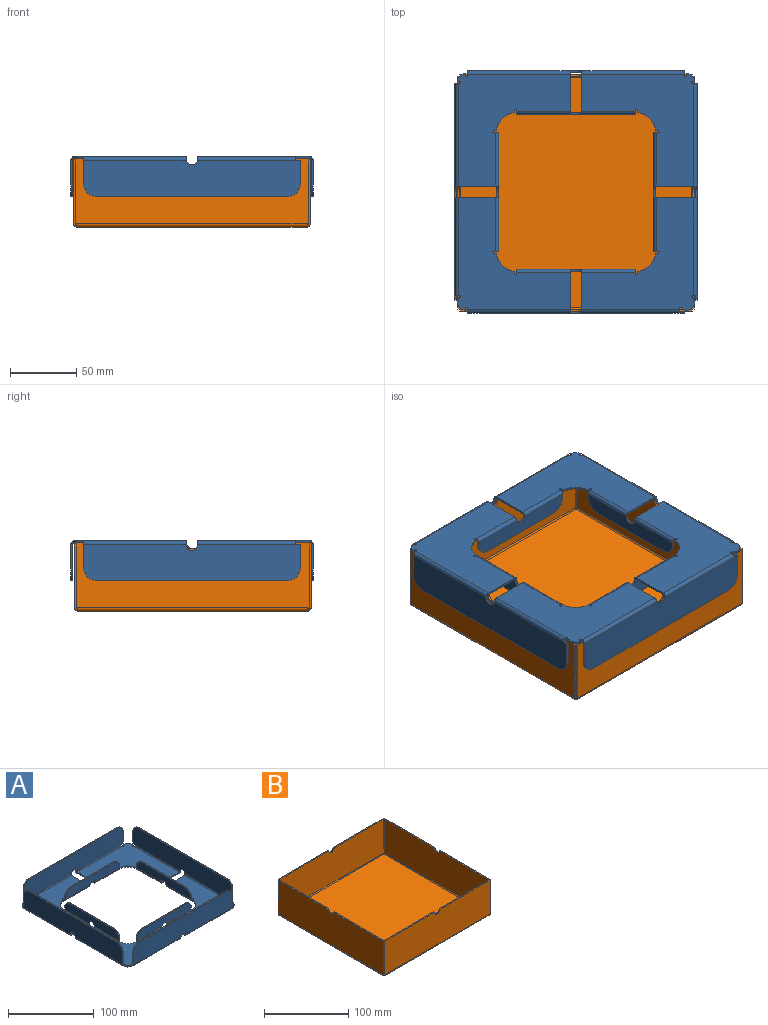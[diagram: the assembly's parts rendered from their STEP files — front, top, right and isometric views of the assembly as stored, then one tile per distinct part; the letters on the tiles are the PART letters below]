
ASSEMBLY  parts=2 mates=1
PART A: 225 faces, bbox 183x183x30 mm
  f0: plane 1.5x0.11mm, normal (-1,0,0), area 0.2mm2, adj f6,f7,f12,f105
  f1: plane 1.5x0.11mm, normal (-1,0,0), area 0.2mm2, adj f51,f52,f56,f96
  f2: cylinder r=15mm len=13.32mm, axis (0,0,-1), area 30.6mm2, adj f6,f7,f21,f24
  f3: plane 2.28x1.5mm, normal (0,1,0), area 3.4mm2, adj f6,f7,f9,f17
  f4: plane 1.5x0.11mm, normal (1,0,0), area 0.2mm2, adj f6,f7,f12,f83
  f5: plane 2.28x1.5mm, normal (1,0,0), area 3.4mm2, adj f6,f7,f8,f15
  f6: plane 85.61x85.5mm, normal (0,0,-1), area 4020mm2, adj f0,f2,f3,f4,f5,f8,f9,f10
  f7: plane 85.61x85.5mm, normal (0,0,1), area 4020mm2, adj f0,f2,f3,f4,f5,f8,f9,f10
  f8: plane 1.5x1mm, normal (0,-1,0), area 1.5mm2, adj f5,f6,f7,f11
  f9: plane 1.5x1mm, normal (-1,0,0), area 1.5mm2, adj f3,f6,f7,f11
  f10: plane 28x1.5mm, normal (-1,0,0), area 42mm2, adj f6,f7,f26,f44
  f11: cylinder r=8mm len=8mm, axis (0,0,-1), area 18.8mm2, adj f6,f7,f8,f9
  f12: plane 28x1.5mm, normal (0,-1,0), area 42mm2, adj f0,f4,f6,f7
  f13: cylinder r=0.8mm len=1.59mm, axis (0,0,1), area 3.8mm2, adj f6,f7,f14,f15
  f14: plane 1.5x0.7mm, normal (0,1,0), area 1.1mm2, adj f6,f7,f13,f84
  f15: plane 1.5x0.7mm, normal (0,-1,0), area 1.1mm2, adj f5,f6,f7,f13
  f16: cylinder r=0.8mm len=1.59mm, axis (0,0,1), area 3.8mm2, adj f6,f7,f17,f18
  f17: plane 1.5x0.7mm, normal (-1,0,0), area 1.1mm2, adj f3,f6,f7,f16
  f18: plane 1.5x0.7mm, normal (1,0,0), area 1.1mm2, adj f6,f7,f16,f25
  f19: plane 1.5x0.7mm, normal (1,0,0), area 1.1mm2, adj f6,f7,f20,f45
  f20: cylinder r=0.8mm len=1.59mm, axis (0,0,1), area 3.8mm2, adj f6,f7,f19,f21
  f21: plane 1.79x1.5mm, normal (-1,0,0), area 2.7mm2, adj f2,f6,f7,f20
  f22: cylinder r=0.8mm len=1.59mm, axis (0,0,1), area 3.8mm2, adj f6,f7,f23,f24
  f23: plane 1.5x0.7mm, normal (0,1,0), area 1.1mm2, adj f6,f7,f22,f104
  f24: plane 1.79x1.5mm, normal (0,-1,0), area 2.7mm2, adj f2,f6,f7,f22
  f25: plane 2.5x2.5mm, normal (1,0,0), area 4.1mm2, adj f18,f27,f28,f30
  f26: plane 2.5x2.5mm, normal (-1,0,0), area 4.1mm2, adj f10,f27,f28,f34
  f27: cylinder r=2.5mm len=73.63mm, axis (1,0,0), area 289.1mm2, adj f6,f25,f26,f36
  f28: cylinder r=1mm len=73.63mm, axis (1,0,0), area 115.7mm2, adj f7,f25,f26,f37
  f29: plane 1.5x0.11mm, normal (0,0,-1), area 0.2mm2, adj f35,f36,f37,f40
  f30: plane 3.87x1.5mm, normal (0,0,-1), area 5.8mm2, adj f25,f33,f36,f37
  f31: plane 17.5x1.5mm, normal (-1,0,0), area 26.2mm2, adj f36,f37,f39,f41
  f32: plane 144x1.5mm, normal (0,0,1), area 216mm2, adj f36,f37,f38,f39
  f33: plane 17.5x1.5mm, normal (1,0,0), area 26.2mm2, adj f30,f36,f37,f38
  f34: plane 1.5x0.11mm, normal (0,0,-1), area 0.2mm2, adj f26,f35,f36,f37
  f35: cylinder r=4.5mm len=8.78mm, axis (0,1,0), area 18.2mm2, adj f29,f34,f36,f37
  f36: plane 164x27.5mm, normal (0,1,0), area 4444.2mm2, adj f27,f29,f30,f31,f32,f33,f34,f35
  f37: plane 164x27.5mm, normal (0,-1,0), area 4444.2mm2, adj f28,f29,f30,f31,f32,f33,f34,f35
  f38: cylinder r=10mm len=10mm, axis (0,1,0), area 23.6mm2, adj f32,f33,f36,f37
  f39: cylinder r=10mm len=10mm, axis (0,1,0), area 23.6mm2, adj f31,f32,f36,f37
  f40: plane 2.5x2.5mm, normal (1,0,0), area 4.1mm2, adj f29,f42,f43,f54
  f41: plane 2.5x2.5mm, normal (-1,0,0), area 4.1mm2, adj f31,f42,f43,f63
  f42: cylinder r=2.5mm len=77.5mm, axis (1,0,0), area 304.3mm2, adj f36,f40,f41,f51
  f43: cylinder r=1mm len=77.5mm, axis (1,0,0), area 121.7mm2, adj f37,f40,f41,f52
  f44: plane 2.5x2.5mm, normal (-1,0,0), area 4.1mm2, adj f10,f46,f47,f73
  f45: plane 2.5x2.5mm, normal (1,0,0), area 4.1mm2, adj f19,f46,f47,f74
  f46: cylinder r=2.5mm len=40.5mm, axis (-1,0,0), area 159mm2, adj f6,f44,f45,f79
  f47: cylinder r=1mm len=40.5mm, axis (-1,0,0), area 63.6mm2, adj f7,f44,f45,f80
  f48: plane 2.28x1.5mm, normal (-1,0,0), area 3.4mm2, adj f51,f52,f53,f67
  f49: cylinder r=8mm len=7.84mm, axis (0,0,-1), area 16.4mm2, adj f51,f52,f53,f65
  f50: cylinder r=15mm len=13.32mm, axis (0,0,-1), area 30.6mm2, adj f51,f52,f59,f62
  f51: plane 85.5x85.45mm, normal (0,0,-1), area 4018.4mm2, adj f1,f42,f48,f49,f50,f53,f54,f55
  f52: plane 85.5x85.45mm, normal (0,0,1), area 4018.4mm2, adj f1,f43,f48,f49,f50,f53,f54,f55
  f53: plane 1.5x1mm, normal (0,-1,0), area 1.5mm2, adj f48,f49,f51,f52
  f54: plane 28x1.5mm, normal (1,0,0), area 42mm2, adj f40,f51,f52,f70
  f55: plane 1.5x0.11mm, normal (1,0,0), area 0.2mm2, adj f51,f52,f56,f100
  f56: plane 28x1.5mm, normal (0,-1,0), area 42mm2, adj f1,f51,f52,f55
  f57: plane 1.5x0.7mm, normal (0,1,0), area 1.1mm2, adj f51,f52,f58,f101
  f58: cylinder r=0.8mm len=1.59mm, axis (0,0,1), area 3.8mm2, adj f51,f52,f57,f59
  f59: plane 1.79x1.5mm, normal (0,-1,0), area 2.7mm2, adj f50,f51,f52,f58
  f60: cylinder r=0.8mm len=1.59mm, axis (0,0,1), area 3.8mm2, adj f51,f52,f61,f62
  f61: plane 1.5x0.7mm, normal (-1,0,0), area 1.1mm2, adj f51,f52,f60,f69
  f62: plane 1.79x1.5mm, normal (1,0,0), area 2.7mm2, adj f50,f51,f52,f60
  f63: plane 1.5x0.7mm, normal (-1,0,0), area 1.1mm2, adj f41,f51,f52,f64
  f64: cylinder r=0.8mm len=1.59mm, axis (0,0,1), area 3.8mm2, adj f51,f52,f63,f65
  f65: plane 1.54x1.5mm, normal (1,0,0), area 2.3mm2, adj f49,f51,f52,f64
  f66: cylinder r=0.8mm len=1.59mm, axis (0,0,1), area 3.8mm2, adj f51,f52,f67,f68
  f67: plane 1.5x0.7mm, normal (0,-1,0), area 1.1mm2, adj f48,f51,f52,f66
  f68: plane 1.5x0.7mm, normal (0,1,0), area 1.1mm2, adj f51,f52,f66,f97
  f69: plane 2.5x2.5mm, normal (-1,0,0), area 4.1mm2, adj f61,f71,f72,f76
  f70: plane 2.5x2.5mm, normal (1,0,0), area 4.1mm2, adj f54,f71,f72,f77
  f71: cylinder r=2.5mm len=40.5mm, axis (-1,0,0), area 159mm2, adj f51,f69,f70,f79
  f72: cylinder r=1mm len=40.5mm, axis (-1,0,0), area 63.6mm2, adj f52,f69,f70,f80
  f73: plane 1.5x0.11mm, normal (0,0,-1), area 0.2mm2, adj f44,f78,f79,f80
  f74: plane 2.5x1.5mm, normal (1,0,0), area 3.8mm2, adj f45,f79,f80,f81
  f75: plane 70x1.5mm, normal (0,0,1), area 105mm2, adj f79,f80,f81,f82
  f76: plane 2.5x1.5mm, normal (-1,0,0), area 3.8mm2, adj f69,f79,f80,f82
  f77: plane 1.5x0.11mm, normal (0,0,-1), area 0.2mm2, adj f70,f78,f79,f80
  f78: cylinder r=4.5mm len=8.78mm, axis (0,-1,0), area 18.2mm2, adj f73,f77,f79,f80
  f79: plane 90x12.5mm, normal (0,-1,0), area 1059.2mm2, adj f46,f71,f73,f74,f75,f76,f77,f78
  f80: plane 90x12.5mm, normal (0,1,0), area 1059.2mm2, adj f47,f72,f73,f74,f75,f76,f77,f78
  f81: cylinder r=10mm len=10mm, axis (0,-1,0), area 23.6mm2, adj f74,f75,f79,f80
  f82: cylinder r=10mm len=10mm, axis (0,-1,0), area 23.6mm2, adj f75,f76,f79,f80
  f83: plane 2.5x2.5mm, normal (0,-1,0), area 4.1mm2, adj f4,f85,f86,f91
  f84: plane 2.5x2.5mm, normal (0,1,0), area 4.1mm2, adj f14,f85,f86,f87
  f85: cylinder r=2.5mm len=73.63mm, axis (0,-1,0), area 289.1mm2, adj f6,f83,f84,f92
  f86: cylinder r=1mm len=73.63mm, axis (0,-1,0), area 115.7mm2, adj f7,f83,f84,f93
  f87: plane 3.87x1.5mm, normal (0,0,-1), area 5.8mm2, adj f84,f88,f92,f93
  f88: plane 17.5x1.5mm, normal (0,1,0), area 26.3mm2, adj f87,f92,f93,f95
  f89: plane 144x1.5mm, normal (0,0,1), area 216mm2, adj f92,f93,f94,f95
  f90: plane 17.5x1.5mm, normal (0,-1,0), area 26.3mm2, adj f92,f93,f94,f108
  f91: cylinder r=4.5mm len=9mm, axis (1,0,0), area 21.2mm2, adj f83,f92,f93,f109
  f92: plane 164x27.5mm, normal (1,0,0), area 4435.3mm2, adj f85,f87,f88,f89,f90,f91,f94,f95
  f93: plane 164x27.5mm, normal (-1,0,0), area 4435.3mm2, adj f86,f87,f88,f89,f90,f91,f94,f95
  f94: cylinder r=10mm len=10mm, axis (1,0,0), area 23.6mm2, adj f89,f90,f92,f93
  f95: cylinder r=10mm len=10mm, axis (1,0,0), area 23.6mm2, adj f88,f89,f92,f93
  f96: plane 2.5x2.5mm, normal (0,-1,0), area 4.1mm2, adj f1,f98,f99,f132
  f97: plane 2.5x2.5mm, normal (0,1,0), area 4.1mm2, adj f68,f98,f99,f128
  f98: cylinder r=2.5mm len=73.63mm, axis (0,-1,0), area 289.1mm2, adj f51,f96,f97,f133
  f99: cylinder r=1mm len=73.63mm, axis (0,-1,0), area 115.7mm2, adj f52,f96,f97,f134
  f100: plane 2.5x2.5mm, normal (0,-1,0), area 4.1mm2, adj f55,f102,f103,f115
  f101: plane 2.5x2.5mm, normal (0,1,0), area 4.1mm2, adj f57,f102,f103,f112
  f102: cylinder r=2.5mm len=40.5mm, axis (0,-1,0), area 159mm2, adj f51,f100,f101,f116
  f103: cylinder r=1mm len=40.5mm, axis (0,-1,0), area 63.6mm2, adj f52,f100,f101,f117
  f104: plane 2.5x2.5mm, normal (0,1,0), area 4.1mm2, adj f23,f106,f107,f122
  f105: plane 2.5x2.5mm, normal (0,-1,0), area 4.1mm2, adj f0,f106,f107,f123
  f106: cylinder r=2.5mm len=40.5mm, axis (0,1,0), area 159mm2, adj f6,f104,f105,f124
  f107: cylinder r=1mm len=40.5mm, axis (0,1,0), area 63.6mm2, adj f7,f104,f105,f125
  f108: plane 2.5x2.5mm, normal (0,-1,0), area 4.1mm2, adj f90,f110,f111,f201
  f109: plane 2.5x2.5mm, normal (0,1,0), area 4.1mm2, adj f91,f110,f111,f142
  f110: cylinder r=2.5mm len=77.5mm, axis (0,-1,0), area 304.3mm2, adj f92,f108,f109,f186
  f111: cylinder r=1mm len=77.5mm, axis (0,-1,0), area 121.7mm2, adj f93,f108,f109,f187
  f112: plane 2.5x1.5mm, normal (0,1,0), area 3.7mm2, adj f101,f116,f117,f119
  f113: plane 70x1.5mm, normal (0,0,1), area 105mm2, adj f116,f117,f118,f119
  f114: plane 2.5x1.5mm, normal (0,-1,0), area 3.7mm2, adj f116,f117,f118,f221
  f115: cylinder r=4.5mm len=9mm, axis (1,0,0), area 21.2mm2, adj f100,f116,f117,f222
  f116: plane 90x12.5mm, normal (1,0,0), area 1050.3mm2, adj f102,f112,f113,f114,f115,f118,f119,f223
  f117: plane 90x12.5mm, normal (-1,0,0), area 1050.3mm2, adj f103,f112,f113,f114,f115,f118,f119,f224
  f118: cylinder r=10mm len=10mm, axis (1,0,0), area 23.6mm2, adj f113,f114,f116,f117
  f119: cylinder r=10mm len=10mm, axis (1,0,0), area 23.6mm2, adj f112,f113,f116,f117
  f120: plane 2.5x1.5mm, normal (0,-1,0), area 3.7mm2, adj f124,f125,f127,f138
  f121: plane 70x1.5mm, normal (0,0,1), area 105mm2, adj f124,f125,f126,f127
  f122: plane 2.5x1.5mm, normal (0,1,0), area 3.7mm2, adj f104,f124,f125,f126
  f123: cylinder r=4.5mm len=9mm, axis (-1,0,0), area 21.2mm2, adj f105,f124,f125,f137
  f124: plane 90x12.5mm, normal (-1,0,0), area 1050.3mm2, adj f106,f120,f121,f122,f123,f126,f127,f139
  f125: plane 90x12.5mm, normal (1,0,0), area 1050.3mm2, adj f107,f120,f121,f122,f123,f126,f127,f140
  f126: cylinder r=10mm len=10mm, axis (-1,0,0), area 23.6mm2, adj f121,f122,f124,f125
  f127: cylinder r=10mm len=10mm, axis (-1,0,0), area 23.6mm2, adj f120,f121,f124,f125
  f128: plane 3.87x1.5mm, normal (0,0,-1), area 5.8mm2, adj f97,f131,f133,f134
  f129: plane 17.5x1.5mm, normal (0,-1,0), area 26.3mm2, adj f133,f134,f136,f217
  f130: plane 144x1.5mm, normal (0,0,1), area 216mm2, adj f133,f134,f135,f136
  f131: plane 17.5x1.5mm, normal (0,1,0), area 26.3mm2, adj f128,f133,f134,f135
  f132: cylinder r=4.5mm len=9mm, axis (-1,0,0), area 21.2mm2, adj f96,f133,f134,f218
  f133: plane 164x27.5mm, normal (-1,0,0), area 4435.3mm2, adj f98,f128,f129,f130,f131,f132,f135,f136
  f134: plane 164x27.5mm, normal (1,0,0), area 4435.3mm2, adj f99,f128,f129,f130,f131,f132,f135,f136
  f135: cylinder r=10mm len=10mm, axis (-1,0,0), area 23.6mm2, adj f130,f131,f133,f134
  f136: cylinder r=10mm len=10mm, axis (-1,0,0), area 23.6mm2, adj f129,f130,f133,f134
  f137: plane 2.5x2.5mm, normal (0,1,0), area 4.1mm2, adj f123,f139,f140,f189
  f138: plane 2.5x2.5mm, normal (0,-1,0), area 4.1mm2, adj f120,f139,f140,f191
  f139: cylinder r=2.5mm len=40.5mm, axis (0,1,0), area 159mm2, adj f124,f137,f138,f186
  f140: cylinder r=1mm len=40.5mm, axis (0,1,0), area 63.6mm2, adj f125,f137,f138,f187
  f141: plane 1.5x0.11mm, normal (1,0,0), area 0.2mm2, adj f145,f146,f149,f222
  f142: plane 1.5x0.11mm, normal (1,0,0), area 0.2mm2, adj f109,f186,f187,f190
  f143: cylinder r=15mm len=13.32mm, axis (0,0,-1), area 30.6mm2, adj f145,f146,f158,f161
  f144: cylinder r=8mm len=6.25mm, axis (0,0,-1), area 14mm2, adj f145,f146,f152,f155
  f145: plane 85.45x85.34mm, normal (0,0,-1), area 4016.9mm2, adj f141,f143,f144,f147,f148,f149,f150,f151
  f146: plane 85.45x85.34mm, normal (0,0,1), area 4016.9mm2, adj f141,f143,f144,f147,f148,f149,f150,f151
  f147: plane 28x1.5mm, normal (1,0,0), area 42mm2, adj f145,f146,f162,f166
  f148: plane 1.5x0.11mm, normal (-1,0,0), area 0.2mm2, adj f145,f146,f149,f218
  f149: plane 28x1.5mm, normal (0,1,0), area 42mm2, adj f141,f145,f146,f148
  f150: plane 1.5x0.7mm, normal (0,-1,0), area 1.1mm2, adj f145,f146,f151,f217
  f151: cylinder r=0.8mm len=1.59mm, axis (0,0,1), area 3.8mm2, adj f145,f146,f150,f152
  f152: plane 1.54x1.5mm, normal (0,1,0), area 2.3mm2, adj f144,f145,f146,f151
  f153: cylinder r=0.8mm len=1.59mm, axis (0,0,1), area 3.8mm2, adj f145,f146,f154,f155
  f154: plane 1.5x0.7mm, normal (-1,0,0), area 1.1mm2, adj f145,f146,f153,f167
  f155: plane 1.54x1.5mm, normal (1,0,0), area 2.3mm2, adj f144,f145,f146,f153
  f156: plane 1.5x0.7mm, normal (-1,0,0), area 1.1mm2, adj f145,f146,f157,f163
  f157: cylinder r=0.8mm len=1.59mm, axis (0,0,1), area 3.8mm2, adj f145,f146,f156,f158
  f158: plane 1.79x1.5mm, normal (1,0,0), area 2.7mm2, adj f143,f145,f146,f157
  f159: cylinder r=0.8mm len=1.59mm, axis (0,0,1), area 3.8mm2, adj f145,f146,f160,f161
  f160: plane 1.5x0.7mm, normal (0,-1,0), area 1.1mm2, adj f145,f146,f159,f221
  f161: plane 1.79x1.5mm, normal (0,1,0), area 2.7mm2, adj f143,f145,f146,f159
  f162: plane 2.5x2.5mm, normal (1,0,0), area 4.1mm2, adj f147,f164,f165,f207
  f163: plane 2.5x2.5mm, normal (-1,0,0), area 4.1mm2, adj f156,f164,f165,f208
  f164: cylinder r=2.5mm len=40.5mm, axis (1,0,0), area 159mm2, adj f145,f162,f163,f213
  f165: cylinder r=1mm len=40.5mm, axis (1,0,0), area 63.6mm2, adj f146,f162,f163,f214
  f166: plane 2.5x2.5mm, normal (1,0,0), area 4.1mm2, adj f147,f168,f169,f174
  f167: plane 2.5x2.5mm, normal (-1,0,0), area 4.1mm2, adj f154,f168,f169,f173
  f168: cylinder r=2.5mm len=77.5mm, axis (1,0,0), area 304.3mm2, adj f145,f166,f167,f176
  f169: cylinder r=1mm len=77.5mm, axis (1,0,0), area 121.7mm2, adj f146,f166,f167,f177
  f170: plane 1.5x0.11mm, normal (0,0,-1), area 0.2mm2, adj f175,f176,f177,f181
  f171: plane 17.5x1.5mm, normal (1,0,0), area 26.3mm2, adj f176,f177,f179,f180
  f172: plane 144x1.5mm, normal (0,0,1), area 216mm2, adj f176,f177,f178,f179
  f173: plane 17.5x1.5mm, normal (-1,0,0), area 26.3mm2, adj f167,f176,f177,f178
  f174: plane 1.5x0.11mm, normal (0,0,-1), area 0.2mm2, adj f166,f175,f176,f177
  f175: cylinder r=4.5mm len=8.78mm, axis (0,-1,0), area 18.2mm2, adj f170,f174,f176,f177
  f176: plane 164x27.5mm, normal (0,-1,0), area 4444.2mm2, adj f168,f170,f171,f172,f173,f174,f175,f178
  f177: plane 164x27.5mm, normal (0,1,0), area 4444.2mm2, adj f169,f170,f171,f172,f173,f174,f175,f178
  f178: cylinder r=10mm len=10mm, axis (0,-1,0), area 23.6mm2, adj f172,f173,f176,f177
  f179: cylinder r=10mm len=10mm, axis (0,-1,0), area 23.6mm2, adj f171,f172,f176,f177
  f180: plane 2.5x2.5mm, normal (1,0,0), area 4.1mm2, adj f171,f182,f183,f197
  f181: plane 2.5x2.5mm, normal (-1,0,0), area 4.1mm2, adj f170,f182,f183,f188
  f182: cylinder r=2.5mm len=77.5mm, axis (1,0,0), area 304.3mm2, adj f176,f180,f181,f186
  f183: cylinder r=1mm len=77.5mm, axis (1,0,0), area 121.7mm2, adj f177,f180,f181,f187
  f184: cylinder r=8mm len=6.25mm, axis (0,0,-1), area 14mm2, adj f186,f187,f199,f202
  f185: cylinder r=15mm len=13.32mm, axis (0,0,-1), area 30.6mm2, adj f186,f187,f193,f196
  f186: plane 85.45x85.34mm, normal (0,0,-1), area 4016.9mm2, adj f110,f139,f142,f182,f184,f185,f188,f189
  f187: plane 85.45x85.34mm, normal (0,0,1), area 4016.9mm2, adj f111,f140,f142,f183,f184,f185,f188,f189
  f188: plane 28x1.5mm, normal (-1,0,0), area 42mm2, adj f181,f186,f187,f204
  f189: plane 1.5x0.11mm, normal (-1,0,0), area 0.2mm2, adj f137,f186,f187,f190
  f190: plane 28x1.5mm, normal (0,1,0), area 42mm2, adj f142,f186,f187,f189
  f191: plane 1.5x0.7mm, normal (0,-1,0), area 1.1mm2, adj f138,f186,f187,f192
  f192: cylinder r=0.8mm len=1.59mm, axis (0,0,1), area 3.8mm2, adj f186,f187,f191,f193
  f193: plane 1.79x1.5mm, normal (0,1,0), area 2.7mm2, adj f185,f186,f187,f192
  f194: cylinder r=0.8mm len=1.59mm, axis (0,0,1), area 3.8mm2, adj f186,f187,f195,f196
  f195: plane 1.5x0.7mm, normal (1,0,0), area 1.1mm2, adj f186,f187,f194,f203
  f196: plane 1.79x1.5mm, normal (-1,0,0), area 2.7mm2, adj f185,f186,f187,f194
  f197: plane 1.5x0.7mm, normal (1,0,0), area 1.1mm2, adj f180,f186,f187,f198
  f198: cylinder r=0.8mm len=1.59mm, axis (0,0,1), area 3.8mm2, adj f186,f187,f197,f199
  f199: plane 1.54x1.5mm, normal (-1,0,0), area 2.3mm2, adj f184,f186,f187,f198
  f200: cylinder r=0.8mm len=1.59mm, axis (0,0,1), area 3.8mm2, adj f186,f187,f201,f202
  f201: plane 1.5x0.7mm, normal (0,-1,0), area 1.1mm2, adj f108,f186,f187,f200
  f202: plane 1.54x1.5mm, normal (0,1,0), area 2.3mm2, adj f184,f186,f187,f200
  f203: plane 2.5x2.5mm, normal (1,0,0), area 4.1mm2, adj f195,f205,f206,f210
  f204: plane 2.5x2.5mm, normal (-1,0,0), area 4.1mm2, adj f188,f205,f206,f211
  f205: cylinder r=2.5mm len=40.5mm, axis (1,0,0), area 159mm2, adj f186,f203,f204,f213
  f206: cylinder r=1mm len=40.5mm, axis (1,0,0), area 63.6mm2, adj f187,f203,f204,f214
  f207: plane 1.5x0.11mm, normal (0,0,-1), area 0.2mm2, adj f162,f212,f213,f214
  f208: plane 2.5x1.5mm, normal (-1,0,0), area 3.8mm2, adj f163,f213,f214,f215
  f209: plane 70x1.5mm, normal (0,0,1), area 105mm2, adj f213,f214,f215,f216
  f210: plane 2.5x1.5mm, normal (1,0,0), area 3.8mm2, adj f203,f213,f214,f216
  f211: plane 1.5x0.11mm, normal (0,0,-1), area 0.2mm2, adj f204,f212,f213,f214
  f212: cylinder r=4.5mm len=8.78mm, axis (0,1,0), area 18.2mm2, adj f207,f211,f213,f214
  f213: plane 90x12.5mm, normal (0,1,0), area 1059.2mm2, adj f164,f205,f207,f208,f209,f210,f211,f212
  f214: plane 90x12.5mm, normal (0,-1,0), area 1059.2mm2, adj f165,f206,f207,f208,f209,f210,f211,f212
  f215: cylinder r=10mm len=10mm, axis (0,1,0), area 23.6mm2, adj f208,f209,f213,f214
  f216: cylinder r=10mm len=10mm, axis (0,1,0), area 23.6mm2, adj f209,f210,f213,f214
  f217: plane 2.5x2.5mm, normal (0,-1,0), area 4.1mm2, adj f129,f150,f219,f220
  f218: plane 2.5x2.5mm, normal (0,1,0), area 4.1mm2, adj f132,f148,f219,f220
  f219: cylinder r=2.5mm len=77.5mm, axis (0,-1,0), area 304.3mm2, adj f133,f145,f217,f218
  f220: cylinder r=1mm len=77.5mm, axis (0,-1,0), area 121.7mm2, adj f134,f146,f217,f218
  f221: plane 2.5x2.5mm, normal (0,-1,0), area 4.1mm2, adj f114,f160,f223,f224
  f222: plane 2.5x2.5mm, normal (0,1,0), area 4.1mm2, adj f115,f141,f223,f224
  f223: cylinder r=2.5mm len=40.5mm, axis (0,-1,0), area 159mm2, adj f116,f145,f221,f222
  f224: cylinder r=1mm len=40.5mm, axis (0,-1,0), area 63.6mm2, adj f117,f146,f221,f222
PART B: 54 faces, bbox 179x179x51.5 mm
  f0: plane 1.5x0.98mm, normal (0,0,-1), area 1.5mm2, adj f2,f7,f8,f51
  f1: plane 83.48x1.5mm, normal (0,0,1), area 125.2mm2, adj f2,f6,f7,f8
  f2: plane 49x1.5mm, normal (1,0,0), area 73.5mm2, adj f0,f1,f7,f8
  f3: plane 1.5x0.98mm, normal (0,0,-1), area 1.5mm2, adj f4,f7,f8,f50
  f4: plane 49x1.5mm, normal (-1,0,0), area 73.5mm2, adj f3,f5,f7,f8
  f5: plane 83.48x1.5mm, normal (0,0,1), area 125.2mm2, adj f4,f6,f7,f8
  f6: cylinder r=4.5mm len=9mm, axis (0,-1,0), area 21.2mm2, adj f1,f5,f7,f8
  f7: plane 175.96x49mm, normal (0,1,0), area 8590.2mm2, adj f0,f1,f2,f3,f4,f5,f6,f52
  f8: plane 175.96x49mm, normal (0,-1,0), area 8590.2mm2, adj f0,f1,f2,f3,f4,f5,f6,f53
  f9: plane 174x174mm, normal (0,0,-1), area 30276mm2, adj f22,f35,f48,f52
  f10: plane 174x174mm, normal (0,0,1), area 30276mm2, adj f23,f36,f49,f53
  f11: plane 1.5x0.98mm, normal (0,0,-1), area 1.5mm2, adj f13,f18,f19,f20
  f12: plane 83.48x1.5mm, normal (0,0,1), area 125.2mm2, adj f13,f17,f18,f19
  f13: plane 49x1.5mm, normal (-1,0,0), area 73.5mm2, adj f11,f12,f18,f19
  f14: plane 1.5x0.98mm, normal (0,0,-1), area 1.5mm2, adj f15,f18,f19,f21
  f15: plane 49x1.5mm, normal (1,0,0), area 73.5mm2, adj f14,f16,f18,f19
  f16: plane 83.48x1.5mm, normal (0,0,1), area 125.2mm2, adj f15,f17,f18,f19
  f17: cylinder r=4.5mm len=9mm, axis (0,-1,0), area 21.2mm2, adj f12,f16,f18,f19
  f18: plane 175.96x49mm, normal (0,-1,0), area 8590.2mm2, adj f11,f12,f13,f14,f15,f16,f17,f22
  f19: plane 175.96x49mm, normal (0,1,0), area 8590.2mm2, adj f11,f12,f13,f14,f15,f16,f17,f23
  f20: plane 2.5x2.5mm, normal (-1,0,0), area 4.1mm2, adj f11,f22,f23,f46
  f21: plane 2.5x2.5mm, normal (1,0,0), area 4.1mm2, adj f14,f22,f23,f33
  f22: cylinder r=2.5mm len=174mm, axis (-1,0,0), area 683.3mm2, adj f9,f18,f20,f21
  f23: cylinder r=1mm len=174mm, axis (-1,0,0), area 273.3mm2, adj f10,f19,f20,f21
  f24: plane 1.5x0.98mm, normal (0,0,-1), area 1.5mm2, adj f26,f31,f32,f33
  f25: plane 83.48x1.5mm, normal (0,0,1), area 125.2mm2, adj f26,f30,f31,f32
  f26: plane 49x1.5mm, normal (0,-1,0), area 73.5mm2, adj f24,f25,f31,f32
  f27: plane 1.5x0.98mm, normal (0,0,-1), area 1.5mm2, adj f28,f31,f32,f34
  f28: plane 49x1.5mm, normal (0,1,0), area 73.5mm2, adj f27,f29,f31,f32
  f29: plane 83.48x1.5mm, normal (0,0,1), area 125.2mm2, adj f28,f30,f31,f32
  f30: cylinder r=4.5mm len=9mm, axis (1,0,0), area 21.2mm2, adj f25,f29,f31,f32
  f31: plane 175.96x49mm, normal (1,0,0), area 8590.2mm2, adj f24,f25,f26,f27,f28,f29,f30,f35
  f32: plane 175.96x49mm, normal (-1,0,0), area 8590.2mm2, adj f24,f25,f26,f27,f28,f29,f30,f36
  f33: plane 2.5x2.5mm, normal (0,-1,0), area 4.1mm2, adj f21,f24,f35,f36
  f34: plane 2.5x2.5mm, normal (0,1,0), area 4.1mm2, adj f27,f35,f36,f51
  f35: cylinder r=2.5mm len=174mm, axis (0,-1,0), area 683.3mm2, adj f9,f31,f33,f34
  f36: cylinder r=1mm len=174mm, axis (0,-1,0), area 273.3mm2, adj f10,f32,f33,f34
  f37: plane 1.5x0.98mm, normal (0,0,-1), area 1.5mm2, adj f39,f44,f45,f47
  f38: plane 83.48x1.5mm, normal (0,0,1), area 125.2mm2, adj f39,f43,f44,f45
  f39: plane 49x1.5mm, normal (0,1,0), area 73.5mm2, adj f37,f38,f44,f45
  f40: plane 1.5x0.98mm, normal (0,0,-1), area 1.5mm2, adj f41,f44,f45,f46
  f41: plane 49x1.5mm, normal (0,-1,0), area 73.5mm2, adj f40,f42,f44,f45
  f42: plane 83.48x1.5mm, normal (0,0,1), area 125.2mm2, adj f41,f43,f44,f45
  f43: cylinder r=4.5mm len=9mm, axis (1,0,0), area 21.2mm2, adj f38,f42,f44,f45
  f44: plane 175.96x49mm, normal (-1,0,0), area 8590.2mm2, adj f37,f38,f39,f40,f41,f42,f43,f48
  f45: plane 175.96x49mm, normal (1,0,0), area 8590.2mm2, adj f37,f38,f39,f40,f41,f42,f43,f49
  f46: plane 2.5x2.5mm, normal (0,-1,0), area 4.1mm2, adj f20,f40,f48,f49
  f47: plane 2.5x2.5mm, normal (0,1,0), area 4.1mm2, adj f37,f48,f49,f50
  f48: cylinder r=2.5mm len=174mm, axis (0,-1,0), area 683.3mm2, adj f9,f44,f46,f47
  f49: cylinder r=1mm len=174mm, axis (0,-1,0), area 273.3mm2, adj f10,f45,f46,f47
  f50: plane 2.5x2.5mm, normal (-1,0,0), area 4.1mm2, adj f3,f47,f52,f53
  f51: plane 2.5x2.5mm, normal (1,0,0), area 4.1mm2, adj f0,f34,f52,f53
  f52: cylinder r=2.5mm len=174mm, axis (-1,0,0), area 683.3mm2, adj f7,f9,f50,f51
  f53: cylinder r=1mm len=174mm, axis (-1,0,0), area 273.3mm2, adj f8,f10,f50,f51
PLACE A rot(axis=(-1,0,0),180deg) t=(0.05,-89.5,50.05)mm
PLACE B at identity
MATE planar A.f37 <-> B.f18  axis (0,1,0) through (0.05,-89.5,35.34)mm
